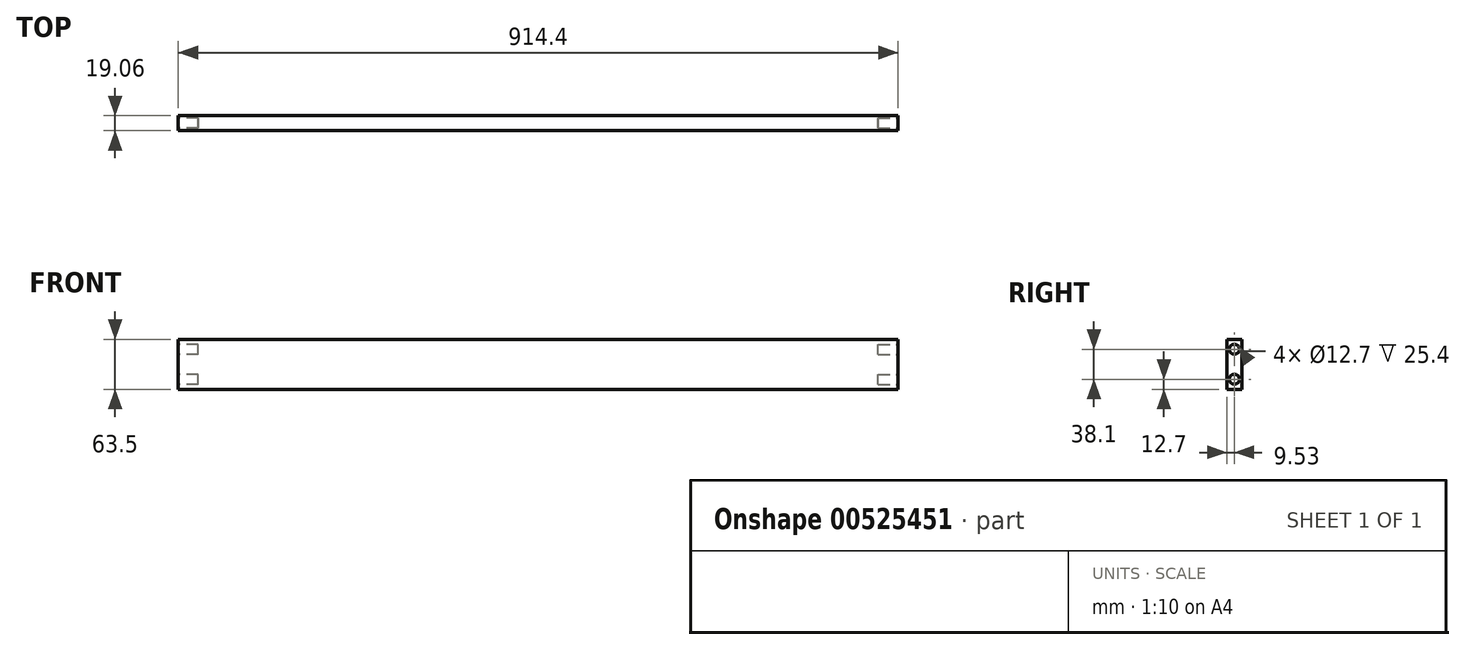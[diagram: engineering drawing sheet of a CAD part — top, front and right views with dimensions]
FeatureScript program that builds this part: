
annotation { "Feature Type Name" : "Feature", "Feature Type Description" : "" }
export const myFeature = defineFeature(function(context is Context, id is Id, definition is map)
    precondition{}
    {
        {
            var Q0;
            Q0=qCreatedBy(makeId("Right.planeOp"),FACE);
            var sketch = newSketch(context, id + "F0", { "sketchPlane" : qUnion([Q0])});
            skLineSegment(sketch, "E0.bottom", {"start": v(9.53, 31.75) * mm, "end": v(-9.53, 31.75) * mm});
            skLineSegment(sketch, "E0.top", {"start": v(9.52, -31.75) * mm, "end": v(-9.52, -31.75) * mm});
            skLineSegment(sketch, "E0.left", {"start": v(9.53, 31.75) * mm, "end": v(9.53, -31.75) * mm});
            skLineSegment(sketch, "E0.right", {"start": v(-9.53, 31.75) * mm, "end": v(-9.53, -31.75) * mm});
            skPoint(sketch, "E0.middle", {"position": v(0, 0) * mm});
            skSolve(sketch);
        }
        {
            var Q0;
            Q0=makeQuery(id+"F0.imprint","IMPRINT",FACE,{"disambiguationData":[TD([[makeQuery(id+"F0.imprint","IMPRINT",EDGE,{"derivedFrom":sQuery(id+"F0.wireOp",EDGE,"E0.bottom")}),1.0]])]});
            extrude(context, id + "F1", {"entities" : qUnion([Q0]), "depth" : 914.4 * mm, "offsetDistance" : 25.4 * mm});
        }
        {
            var Q0;
            Q0=qCreatedBy(makeId("Right.planeOp"),FACE);
            var sketch = newSketch(context, id + "F2", { "sketchPlane" : qUnion([Q0])});
            skCircle(sketch, "E1", {"center": v(0, 19.05) * mm, "radius": 6.35 * mm});
            skCircle(sketch, "E2", {"center": v(0, -19.05) * mm, "radius": 6.35 * mm});
            skLineSegment(sketch, "E3", {"start": v(0, 19.05) * mm, "end": v(0, 0) * mm, "construction": true});
            skLineSegment(sketch, "E4", {"start": v(0, 0) * mm, "end": v(0, -19.05) * mm, "construction": true});
            skSolve(sketch);
        }
        {
            var Q0;
            Q0 = qSketchRegion(id + "F2", true);
            extrude(context, id + "F3", {"entities" : qUnion([Q0]), "operationType" : NewBodyOperationType.REMOVE, "depth" : 25.4 * mm, "offsetDistance" : 25.4 * mm});
        }
        {
            var Q0;
            Q0=makeQuery(id+"F1.opExtrude","CAP_FACE",FACE,{"disambiguationData":[OSD([sQuery(id+"F0.wireOp",EDGE,"E0.bottom"),sQuery(id+"F0.wireOp",EDGE,"E0.top"),sQuery(id+"F0.wireOp",EDGE,"E0.left"),sQuery(id+"F0.wireOp",EDGE,"E0.right")])],"isStart":false});
            var sketch = newSketch(context, id + "F4", { "sketchPlane" : qUnion([Q0])});
            skCircle(sketch, "E5", {"center": v(0, 19.05) * mm, "radius": 6.35 * mm});
            skCircle(sketch, "E6", {"center": v(0, -19.05) * mm, "radius": 6.35 * mm});
            skLineSegment(sketch, "E7", {"start": v(0, 19.05) * mm, "end": v(0, 0) * mm, "construction": true});
            skLineSegment(sketch, "E8", {"start": v(0, 0) * mm, "end": v(0, -19.05) * mm, "construction": true});
            skSolve(sketch);
        }
        {
            var Q0;
            Q0 = qSketchRegion(id + "F4", true);
            extrude(context, id + "F5", {"entities" : qUnion([Q0]), "operationType" : NewBodyOperationType.REMOVE, "oppositeDirection" : true, "depth" : 25.4 * mm, "offsetDistance" : 25.4 * mm});
        }
    });
